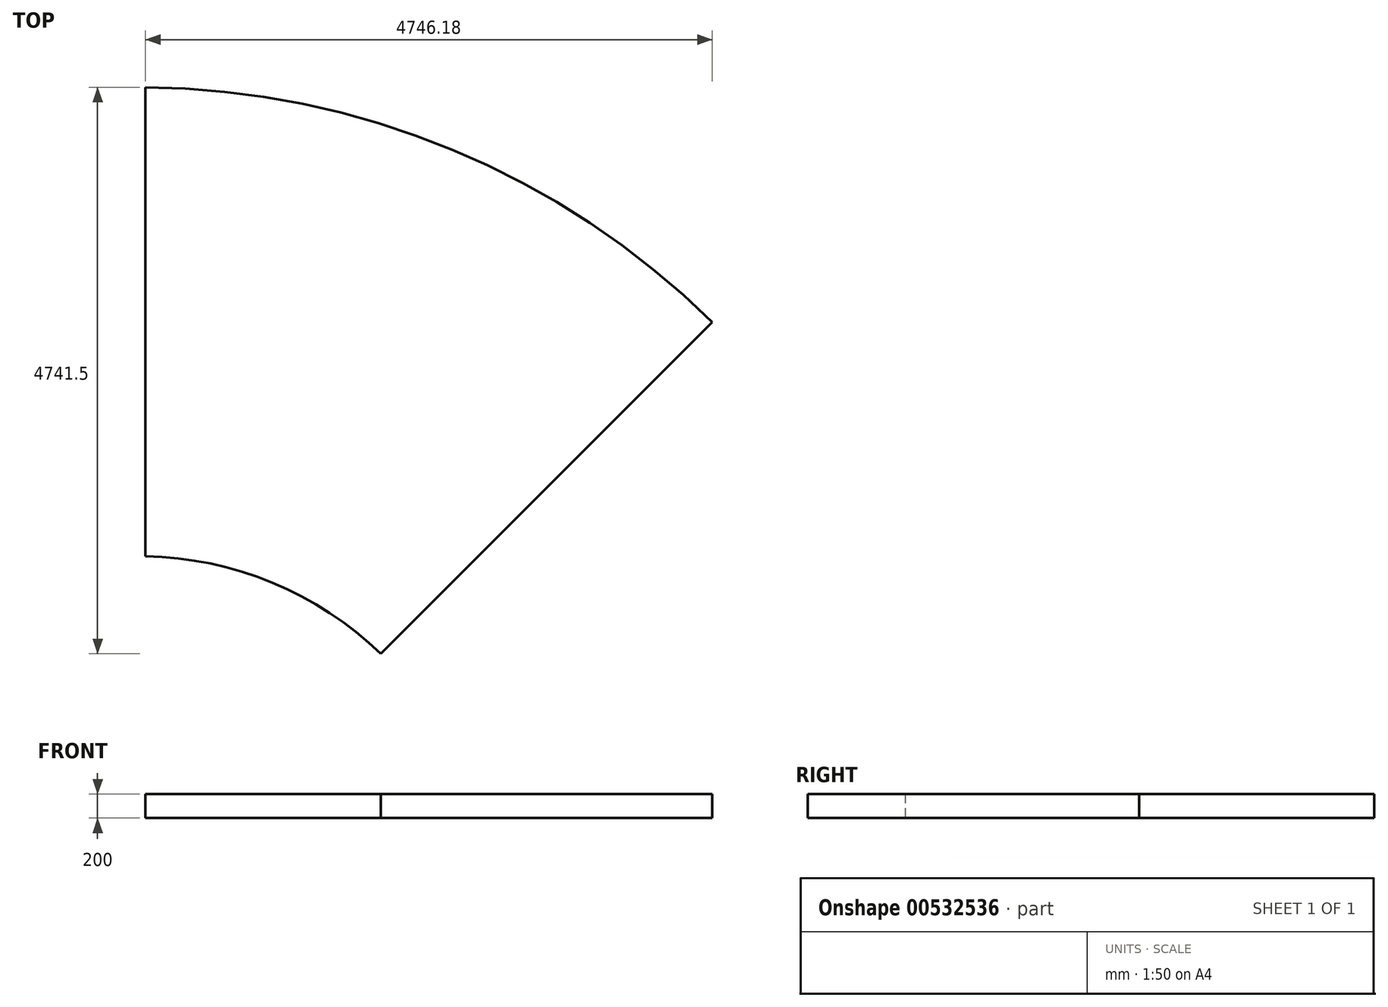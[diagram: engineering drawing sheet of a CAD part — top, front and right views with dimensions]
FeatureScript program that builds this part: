
annotation { "Feature Type Name" : "Feature", "Feature Type Description" : "" }
export const myFeature = defineFeature(function(context is Context, id is Id, definition is map)
    precondition{}
    {
        {
            var Q0;
            Q0=qCreatedBy(makeId("Top.planeOp"),FACE);
            var sketch = newSketch(context, id + "F0", { "sketchPlane" : qUnion([Q0])});
            skArc(sketch, "E0", {"start": v(-2020.91, 2020.91) * mm, "mid": v(-1093.7, -2640.45) * mm, "end": v(2858, 0) * mm});
            skArc(sketch, "E1", {"start": v(-4867.02, 4867.02) * mm, "mid": v(-2634.01, -6359.06) * mm, "end": v(6883, 0) * mm});
            skLineSegment(sketch, "E2", {"start": v(0, 2858) * mm, "end": v(0, 6883) * mm});
            skLineSegment(sketch, "E3.1.0", {"start": v(-2020.91, 2020.91) * mm, "end": v(-4867.02, 4867.02) * mm});
            skLineSegment(sketch, "E3.2.0", {"start": v(-2858, 0) * mm, "end": v(-6883, 0) * mm});
            skLineSegment(sketch, "E3.3.0", {"start": v(-2020.91, -2020.91) * mm, "end": v(-4867.02, -4867.02) * mm});
            skLineSegment(sketch, "E3.4.0", {"start": v(0, -2858) * mm, "end": v(0, -6883) * mm});
            skLineSegment(sketch, "E3.5.0", {"start": v(2020.91, -2020.91) * mm, "end": v(4867.02, -4867.02) * mm});
            skLineSegment(sketch, "E3.6.0", {"start": v(2858, 0) * mm, "end": v(6883, 0) * mm});
            skLineSegment(sketch, "E3.7.0", {"start": v(2020.91, 2020.91) * mm, "end": v(4867.02, 4867.02) * mm});
            skPoint(sketch, "E4", {"position": v(0, 2858) * mm});
            skPoint(sketch, "E5", {"position": v(2020.91, 2020.91) * mm});
            skPoint(sketch, "E6", {"position": v(4867.02, 4867.02) * mm});
            skPoint(sketch, "E7", {"position": v(0, 6883) * mm});
            skArc(sketch, "E8.trimOffspring", {"start": v(2020.91, 2020.91) * mm, "mid": v(1093.7, 2640.45) * mm, "end": v(0, 2858) * mm});
            skArc(sketch, "E9.trimOffspring", {"start": v(4867.02, 4867.02) * mm, "mid": v(2634.01, 6359.06) * mm, "end": v(0, 6883) * mm});
            skLineSegment(sketch, "E10.0", {"start": v(50, 2907.57) * mm, "end": v(50, 6832.82) * mm});
            skArc(sketch, "E10.1", {"start": v(2020.6, 2091.32) * mm, "mid": v(1112.84, 2686.64) * mm, "end": v(50, 2907.57) * mm});
            skLineSegment(sketch, "E10.2", {"start": v(2020.6, 2091.32) * mm, "end": v(4796.18, 4866.89) * mm});
            skArc(sketch, "E10.3", {"start": v(4796.18, 4866.89) * mm, "mid": v(2614.88, 6312.87) * mm, "end": v(50, 6832.82) * mm});
            skSolve(sketch);
        }
        {
            var Q0;
            Q0=makeQuery(id+"F0.imprint","IMPRINT",FACE,{"disambiguationData":[TD([[makeQuery(id+"F0.imprint","IMPRINT",EDGE,{"derivedFrom":sQuery(id+"F0.wireOp",EDGE,"E10.0")}),-1.0]])]});
            extrude(context, id + "F1", {"entities" : qUnion([Q0]), "depth" : 200 * mm, "offsetDistance" : 25 * mm});
        }
    });
